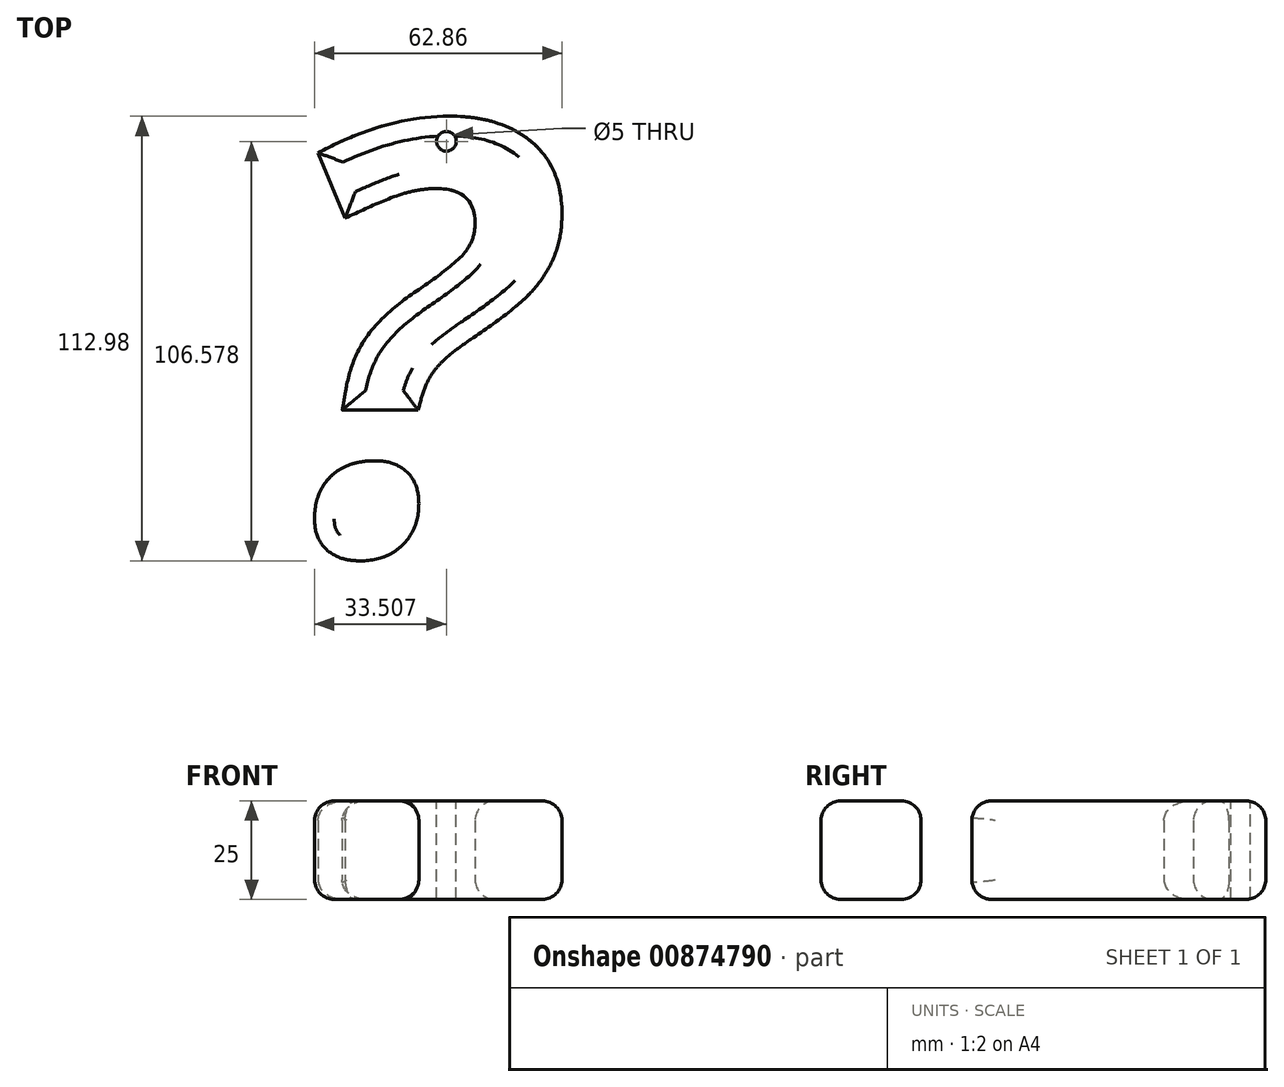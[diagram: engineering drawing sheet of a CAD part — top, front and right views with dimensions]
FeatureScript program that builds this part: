
annotation { "Feature Type Name" : "Feature", "Feature Type Description" : "" }
export const myFeature = defineFeature(function(context is Context, id is Id, definition is map)
    precondition{}
    {
        {
            var Q0;
            Q0=qCreatedBy(makeId("Top.planeOp"),FACE);
            var sketch = newSketch(context, id + "F0", { "sketchPlane" : qUnion([Q0])});
            skText(sketch, "E0", { "text": "? \n", "fontName": "OpenSans-BoldItalic.ttf"});
            const initialGuessF0  = {"E0": [-0.08072, -0.0425, 1, 0, 0.11035]};
            skSetInitialGuess(sketch, initialGuessF0);
            skSolve(sketch);
        }
        {
            var Q0;
            Q0 = qSketchRegion(id + "F0", true);
            extrude(context, id + "F1", {"entities" : qUnion([Q0]), "depth" : 25 * mm, "offsetDistance" : 25 * mm});
        }
        {
            var Q0;
            Q0=makeQuery(id+"F1.opExtrude","CAP_FACE",FACE,{"disambiguationData":[OSD([sQuery(id+"F0.wireOp",EDGE,"E0.sketch_text.stroke-0"),sQuery(id+"F0.wireOp",EDGE,"E0.sketch_text.stroke-1"),sQuery(id+"F0.wireOp",EDGE,"E0.sketch_text.stroke-2"),sQuery(id+"F0.wireOp",EDGE,"E0.sketch_text.stroke-3"),sQuery(id+"F0.wireOp",EDGE,"E0.sketch_text.stroke-4"),sQuery(id+"F0.wireOp",EDGE,"E0.sketch_text.stroke-5"),sQuery(id+"F0.wireOp",EDGE,"E0.sketch_text.stroke-6"),sQuery(id+"F0.wireOp",EDGE,"E0.sketch_text.stroke-7"),sQuery(id+"F0.wireOp",EDGE,"E0.sketch_text.stroke-8"),sQuery(id+"F0.wireOp",EDGE,"E0.sketch_text.stroke-9"),sQuery(id+"F0.wireOp",EDGE,"E0.sketch_text.stroke-10"),sQuery(id+"F0.wireOp",EDGE,"E0.sketch_text.stroke-11"),sQuery(id+"F0.wireOp",EDGE,"E0.sketch_text.stroke-12"),sQuery(id+"F0.wireOp",EDGE,"E0.sketch_text.stroke-13"),sQuery(id+"F0.wireOp",EDGE,"E0.sketch_text.stroke-14"),sQuery(id+"F0.wireOp",EDGE,"E0.sketch_text.stroke-15"),sQuery(id+"F0.wireOp",EDGE,"E0.sketch_text.stroke-16"),sQuery(id+"F0.wireOp",EDGE,"E0.sketch_text.stroke-17"),sQuery(id+"F0.wireOp",EDGE,"E0.sketch_text.stroke-18")])],"isStart":false});
            fillet(context, id + "F2", {"entities" : qUnion([Q0]), "radius" : 5 * mm, "tangentPropagation" : true, "allowEdgeOverflow" : false});
        }
        {
            var Q0;
            Q0=makeQuery(id+"F1.opExtrude","CAP_FACE",FACE,{"disambiguationData":[OSD([sQuery(id+"F0.wireOp",EDGE,"E0.sketch_text.stroke-0"),sQuery(id+"F0.wireOp",EDGE,"E0.sketch_text.stroke-1"),sQuery(id+"F0.wireOp",EDGE,"E0.sketch_text.stroke-2"),sQuery(id+"F0.wireOp",EDGE,"E0.sketch_text.stroke-3"),sQuery(id+"F0.wireOp",EDGE,"E0.sketch_text.stroke-4"),sQuery(id+"F0.wireOp",EDGE,"E0.sketch_text.stroke-5"),sQuery(id+"F0.wireOp",EDGE,"E0.sketch_text.stroke-6"),sQuery(id+"F0.wireOp",EDGE,"E0.sketch_text.stroke-7"),sQuery(id+"F0.wireOp",EDGE,"E0.sketch_text.stroke-8"),sQuery(id+"F0.wireOp",EDGE,"E0.sketch_text.stroke-9"),sQuery(id+"F0.wireOp",EDGE,"E0.sketch_text.stroke-10"),sQuery(id+"F0.wireOp",EDGE,"E0.sketch_text.stroke-11"),sQuery(id+"F0.wireOp",EDGE,"E0.sketch_text.stroke-12"),sQuery(id+"F0.wireOp",EDGE,"E0.sketch_text.stroke-13"),sQuery(id+"F0.wireOp",EDGE,"E0.sketch_text.stroke-14"),sQuery(id+"F0.wireOp",EDGE,"E0.sketch_text.stroke-15"),sQuery(id+"F0.wireOp",EDGE,"E0.sketch_text.stroke-16"),sQuery(id+"F0.wireOp",EDGE,"E0.sketch_text.stroke-17"),sQuery(id+"F0.wireOp",EDGE,"E0.sketch_text.stroke-18")])],"isStart":true});
            fillet(context, id + "F3", {"entities" : qUnion([Q0]), "radius" : 5 * mm, "tangentPropagation" : true, "allowEdgeOverflow" : false});
        }
        {
            var Q0;
            Q0=makeQuery(id+"F1.opExtrude","CAP_FACE",FACE,{"disambiguationData":[OSD([sQuery(id+"F0.wireOp",EDGE,"E0.sketch_text.stroke-19"),sQuery(id+"F0.wireOp",EDGE,"E0.sketch_text.stroke-20"),sQuery(id+"F0.wireOp",EDGE,"E0.sketch_text.stroke-21"),sQuery(id+"F0.wireOp",EDGE,"E0.sketch_text.stroke-22"),sQuery(id+"F0.wireOp",EDGE,"E0.sketch_text.stroke-23"),sQuery(id+"F0.wireOp",EDGE,"E0.sketch_text.stroke-24"),sQuery(id+"F0.wireOp",EDGE,"E0.sketch_text.stroke-25"),sQuery(id+"F0.wireOp",EDGE,"E0.sketch_text.stroke-26")])],"isStart":true});
            fillet(context, id + "F4", {"entities" : qUnion([Q0]), "radius" : 5 * mm, "tangentPropagation" : true, "allowEdgeOverflow" : false});
        }
        {
            var Q0;
            Q0=makeQuery(id+"F1.opExtrude","CAP_FACE",FACE,{"disambiguationData":[OSD([sQuery(id+"F0.wireOp",EDGE,"E0.sketch_text.stroke-19"),sQuery(id+"F0.wireOp",EDGE,"E0.sketch_text.stroke-20"),sQuery(id+"F0.wireOp",EDGE,"E0.sketch_text.stroke-21"),sQuery(id+"F0.wireOp",EDGE,"E0.sketch_text.stroke-22"),sQuery(id+"F0.wireOp",EDGE,"E0.sketch_text.stroke-23"),sQuery(id+"F0.wireOp",EDGE,"E0.sketch_text.stroke-24"),sQuery(id+"F0.wireOp",EDGE,"E0.sketch_text.stroke-25"),sQuery(id+"F0.wireOp",EDGE,"E0.sketch_text.stroke-26")])],"isStart":false});
            fillet(context, id + "F5", {"entities" : qUnion([Q0]), "radius" : 5 * mm, "tangentPropagation" : true, "allowEdgeOverflow" : false});
        }
        {
            var Q0;
            Q0=makeQuery(id+"F1.opExtrude","CAP_FACE",FACE,{"disambiguationData":[OSD([sQuery(id+"F0.wireOp",EDGE,"E0.sketch_text.stroke-0"),sQuery(id+"F0.wireOp",EDGE,"E0.sketch_text.stroke-1"),sQuery(id+"F0.wireOp",EDGE,"E0.sketch_text.stroke-2"),sQuery(id+"F0.wireOp",EDGE,"E0.sketch_text.stroke-3"),sQuery(id+"F0.wireOp",EDGE,"E0.sketch_text.stroke-4"),sQuery(id+"F0.wireOp",EDGE,"E0.sketch_text.stroke-5"),sQuery(id+"F0.wireOp",EDGE,"E0.sketch_text.stroke-6"),sQuery(id+"F0.wireOp",EDGE,"E0.sketch_text.stroke-7"),sQuery(id+"F0.wireOp",EDGE,"E0.sketch_text.stroke-8"),sQuery(id+"F0.wireOp",EDGE,"E0.sketch_text.stroke-9"),sQuery(id+"F0.wireOp",EDGE,"E0.sketch_text.stroke-10"),sQuery(id+"F0.wireOp",EDGE,"E0.sketch_text.stroke-11"),sQuery(id+"F0.wireOp",EDGE,"E0.sketch_text.stroke-12"),sQuery(id+"F0.wireOp",EDGE,"E0.sketch_text.stroke-13"),sQuery(id+"F0.wireOp",EDGE,"E0.sketch_text.stroke-14"),sQuery(id+"F0.wireOp",EDGE,"E0.sketch_text.stroke-15"),sQuery(id+"F0.wireOp",EDGE,"E0.sketch_text.stroke-16"),sQuery(id+"F0.wireOp",EDGE,"E0.sketch_text.stroke-17"),sQuery(id+"F0.wireOp",EDGE,"E0.sketch_text.stroke-18")])],"isStart":false});
            var sketch = newSketch(context, id + "F6", { "sketchPlane" : qUnion([Q0])});
            skCircle(sketch, "E1", {"center": v(-34.78, 62.07) * mm, "radius": 3 * mm});
            skSolve(sketch);
        }
        {
            var Q0;
            Q0=sQuery(id+"F6.wireOp",VERTEX,"E1.center");
            var Q1;
            Q1=makeQuery(id+"F1.opExtrude","SWEPT_BODY",BODY,{"disambiguationData":[OSD([sQuery(id+"F0.wireOp",EDGE,"E0.sketch_text.stroke-0"),sQuery(id+"F0.wireOp",EDGE,"E0.sketch_text.stroke-1"),sQuery(id+"F0.wireOp",EDGE,"E0.sketch_text.stroke-2"),sQuery(id+"F0.wireOp",EDGE,"E0.sketch_text.stroke-3"),sQuery(id+"F0.wireOp",EDGE,"E0.sketch_text.stroke-4"),sQuery(id+"F0.wireOp",EDGE,"E0.sketch_text.stroke-5"),sQuery(id+"F0.wireOp",EDGE,"E0.sketch_text.stroke-6"),sQuery(id+"F0.wireOp",EDGE,"E0.sketch_text.stroke-7"),sQuery(id+"F0.wireOp",EDGE,"E0.sketch_text.stroke-8"),sQuery(id+"F0.wireOp",EDGE,"E0.sketch_text.stroke-9"),sQuery(id+"F0.wireOp",EDGE,"E0.sketch_text.stroke-10"),sQuery(id+"F0.wireOp",EDGE,"E0.sketch_text.stroke-11"),sQuery(id+"F0.wireOp",EDGE,"E0.sketch_text.stroke-12"),sQuery(id+"F0.wireOp",EDGE,"E0.sketch_text.stroke-13"),sQuery(id+"F0.wireOp",EDGE,"E0.sketch_text.stroke-14"),sQuery(id+"F0.wireOp",EDGE,"E0.sketch_text.stroke-15"),sQuery(id+"F0.wireOp",EDGE,"E0.sketch_text.stroke-16"),sQuery(id+"F0.wireOp",EDGE,"E0.sketch_text.stroke-17"),sQuery(id+"F0.wireOp",EDGE,"E0.sketch_text.stroke-18")])]});
            hole(context, id + "F7", {"style" : HoleStyle.SIMPLE, "endStyle" : HoleEndStyle.THROUGH, "holeDiameter" : 5 * mm, "majorDiameter" : 5 * mm, "isTappedThrough" : true, "tappedDepth" : 12 * mm, "tapClearance" : 3, "locations" : qUnion([Q0]), "scope" : qUnion([Q1])});
        }
    });
